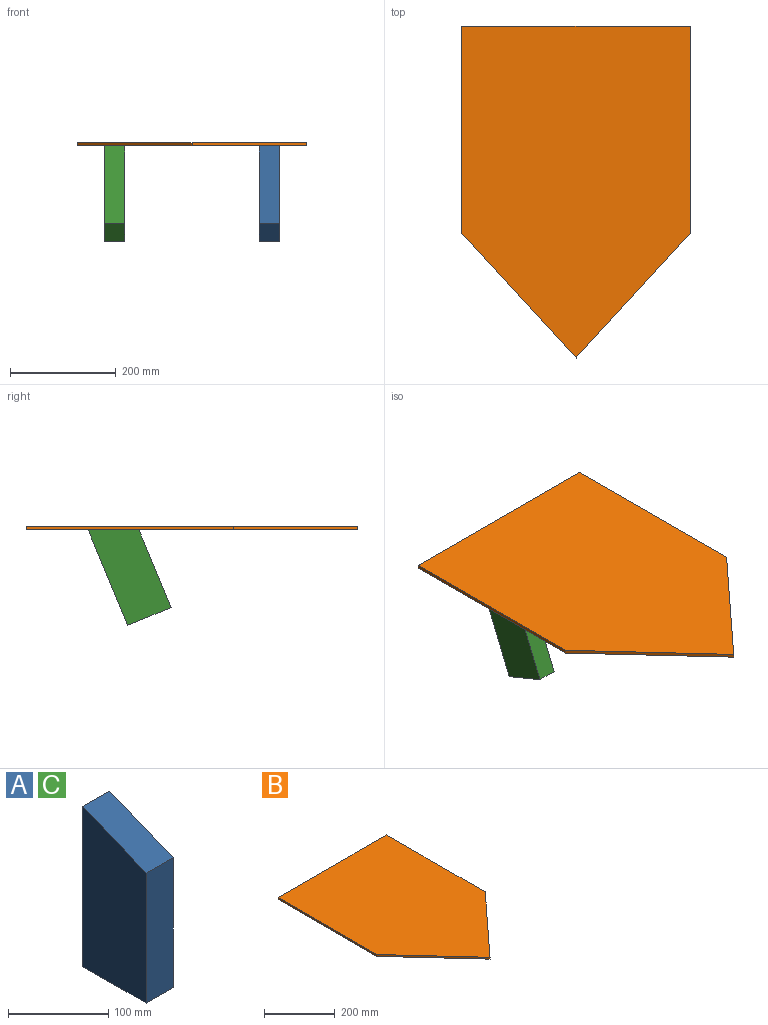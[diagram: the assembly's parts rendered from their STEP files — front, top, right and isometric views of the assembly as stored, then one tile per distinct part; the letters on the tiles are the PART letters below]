
ASSEMBLY  parts=3 mates=2
PART A: 6 faces, bbox 38.1x88.9x195.6 mm
  f0: plane 88.9x38.1mm, normal (0,-0.38,0.92), area 3666.2mm2, adj f1,f3,f4,f5
  f1: plane 158.75x38.1mm, normal (0,-1,0), area 6048.4mm2, adj f0,f2,f4,f5
  f2: plane 88.9x38.1mm, normal (0,0,-1), area 3387.1mm2, adj f1,f3,f4,f5
  f3: plane 195.57x38.1mm, normal (0,1,0), area 7451.4mm2, adj f0,f2,f4,f5
  f4: plane 195.57x88.9mm, normal (1,0,0), area 15749.7mm2, adj f0,f1,f2,f3
  f5: plane 195.57x88.9mm, normal (-1,0,0), area 15749.7mm2, adj f0,f1,f2,f3
PART B: 7 faces, bbox 431.8x628.7x6.4 mm
  f0: plane 393.7x6.35mm, normal (-1,0,0), area 2500mm2, adj f1,f4,f5,f6
  f1: plane 234.95x215.9mm, normal (-0.74,-0.68,0), area 2026.2mm2, adj f0,f2,f5,f6
  f2: plane 234.95x215.9mm, normal (0.74,-0.68,0), area 2026.2mm2, adj f1,f3,f5,f6
  f3: plane 393.7x6.35mm, normal (1,0,0), area 2500mm2, adj f2,f4,f5,f6
  f4: plane 431.8x6.35mm, normal (0,1,0), area 2741.9mm2, adj f0,f3,f5,f6
  f5: plane 628.65x431.8mm, normal (0,0,1), area 220725.4mm2, adj f0,f1,f2,f3,f4
  f6: plane 628.65x431.8mm, normal (0,0,-1), area 220725.4mm2, adj f0,f1,f2,f3,f4
PART C: same geometry as A
PLACE A rot(axis=(-1,0,0),22.5deg) t=(50.06,223.29,133.95)mm
PLACE B t=(-76.94,110.17,228.7)mm
PLACE C rot(axis=(-1,0,0),22.5deg) t=(-242.04,223.29,133.95)mm
MATE fastened A.f0 <-> B.f6  axis (0,0,1) through (88.16,306.64,228.7)mm
MATE fastened C.f0 <-> B.f6  axis (0,0,1) through (-242.04,306.64,228.7)mm
